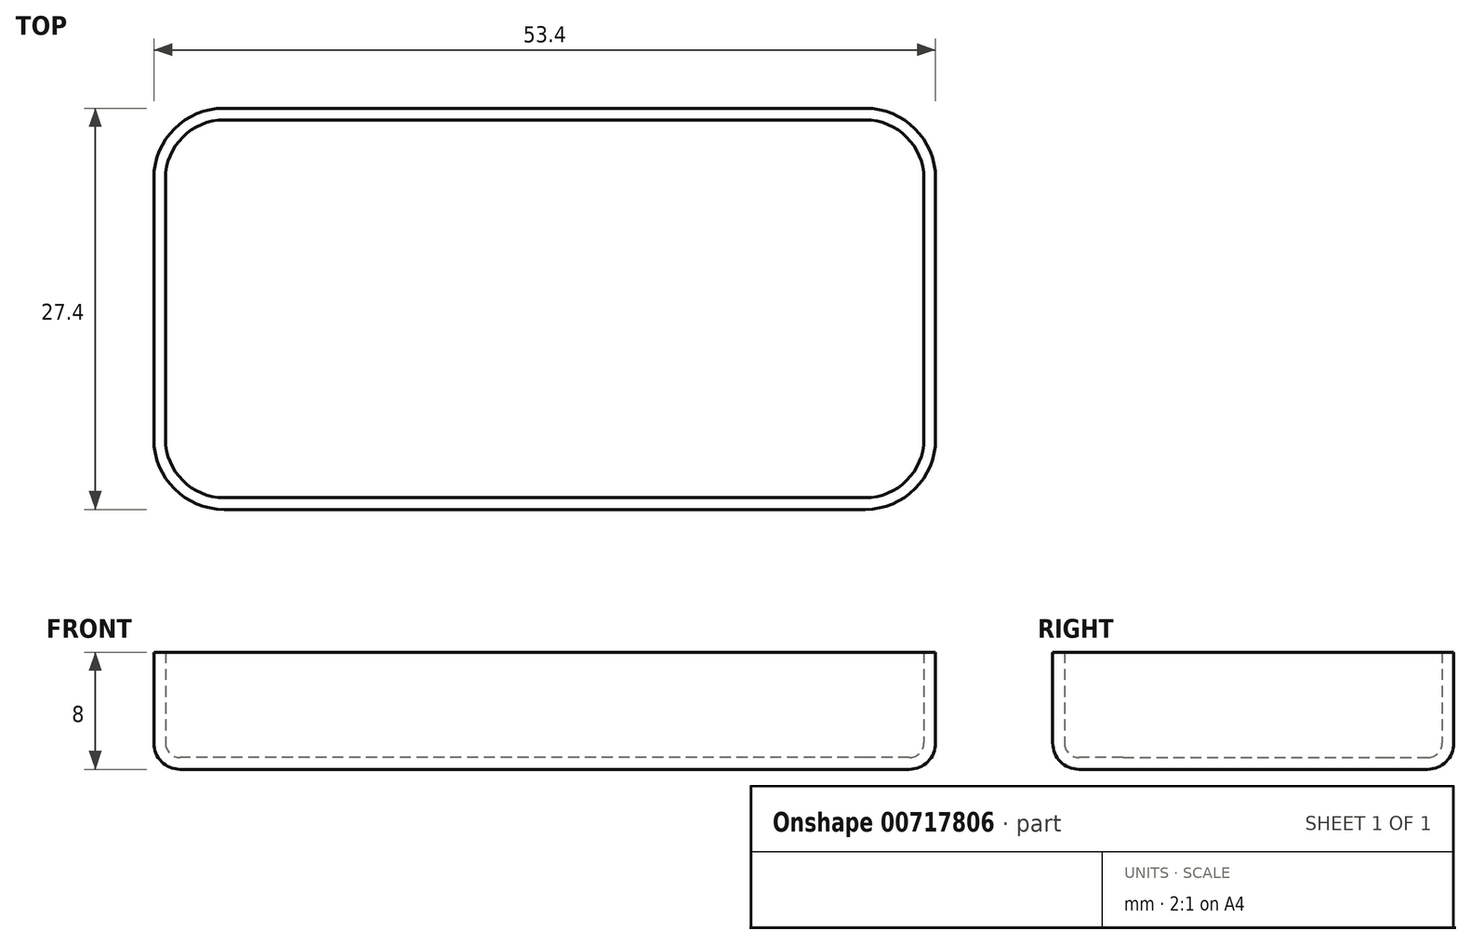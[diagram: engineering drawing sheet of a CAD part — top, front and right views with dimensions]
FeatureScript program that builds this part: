
annotation { "Feature Type Name" : "Feature", "Feature Type Description" : "" }
export const myFeature = defineFeature(function(context is Context, id is Id, definition is map)
    precondition{}
    {
        {
            var Q0;
            Q0=qCreatedBy(makeId("Top.planeOp"),FACE);
            var sketch = newSketch(context, id + "F0", { "sketchPlane" : qUnion([Q0])});
            skLineSegment(sketch, "E0.bottom", {"start": v(26.7, -13.7) * mm, "end": v(-26.7, -13.7) * mm});
            skLineSegment(sketch, "E0.top", {"start": v(26.7, 13.7) * mm, "end": v(-26.7, 13.7) * mm});
            skLineSegment(sketch, "E0.left", {"start": v(26.7, -13.7) * mm, "end": v(26.7, 13.7) * mm});
            skLineSegment(sketch, "E0.right", {"start": v(-26.7, -13.7) * mm, "end": v(-26.7, 13.7) * mm});
            skPoint(sketch, "E0.middle", {"position": v(0, 0) * mm});
            skLineSegment(sketch, "E1.bottom", {"start": v(-25.9, 12.9) * mm, "end": v(25.9, 12.9) * mm});
            skLineSegment(sketch, "E1.top", {"start": v(-25.9, -12.9) * mm, "end": v(25.9, -12.9) * mm});
            skLineSegment(sketch, "E1.left", {"start": v(-25.9, 12.9) * mm, "end": v(-25.9, -12.9) * mm});
            skLineSegment(sketch, "E1.right", {"start": v(25.9, 12.9) * mm, "end": v(25.9, -12.9) * mm});
            skSolve(sketch);
        }
        {
            var Q0;
            Q0=qSketchRegion(id+"F0",true);
            var Q1;
            Q1=makeQuery(id+"F0.imprint","IMPRINT",FACE,{"disambiguationData":[TD([[makeQuery(id+"F0.imprint","IMPRINT",EDGE,{"derivedFrom":sQuery(id+"F0.wireOp",EDGE,"E1.bottom")}),-1.0]])]});
            extrude(context, id + "F1", {"entities" : qUnion([Q0, Q1]), "depth" : .8 * mm, "offsetDistance" : 25 * mm});
        }
        {
            var Q0;
            Q0=makeQuery(id+"F0.imprint","IMPRINT",FACE,{"disambiguationData":[TD([[makeQuery(id+"F0.imprint","IMPRINT",EDGE,{"derivedFrom":sQuery(id+"F0.wireOp",EDGE,"E0.bottom")}),-1.0]])]});
            extrude(context, id + "F2", {"entities" : qUnion([Q0]), "operationType" : NewBodyOperationType.ADD, "depth" : 8 * mm, "offsetDistance" : 25 * mm});
        }
        {
            var Q0;
            Q0=makeQuery(id+"F2.opExtrude","SWEPT_EDGE",EDGE,{"disambiguationData":[OSD([sQuery(id+"F0.wireOp",EDGE,"E1.bottom"),sQuery(id+"F0.wireOp",EDGE,"E1.left")])]});
            var Q1;
            Q1=makeQuery(id+"F2.opExtrude","SWEPT_EDGE",EDGE,{"disambiguationData":[OSD([sQuery(id+"F0.wireOp",EDGE,"E1.bottom"),sQuery(id+"F0.wireOp",EDGE,"E1.right")])]});
            var Q2;
            Q2=makeQuery(id+"F2.opExtrude","SWEPT_EDGE",EDGE,{"disambiguationData":[OSD([sQuery(id+"F0.wireOp",EDGE,"E1.top"),sQuery(id+"F0.wireOp",EDGE,"E1.right")])]});
            var Q3;
            Q3=makeQuery(id+"F2.opExtrude","SWEPT_EDGE",EDGE,{"disambiguationData":[OSD([sQuery(id+"F0.wireOp",EDGE,"E1.top"),sQuery(id+"F0.wireOp",EDGE,"E1.left")])]});
            fillet(context, id + "F3", {"entities" : qUnion([Q0, Q1, Q2, Q3]), "radius" : 4 * mm, "tangentPropagation" : true, "allowEdgeOverflow" : false});
        }
        {
            var Q0;
            {var subQ0=sQuery(id+"F0.wireOp",EDGE,"E0.left");var subQ1=sQuery(id+"F0.wireOp",EDGE,"E0.top");Q0=makeQuery(id+"F2.boolean.opBoolean","MERGE",EDGE,{"derivedFrom":[makeQuery(id+"F1.opExtrude","SWEPT_EDGE",EDGE,{"disambiguationData":[OSD([subQ1,subQ0])]}),makeQuery(id+"F2.opExtrude","SWEPT_EDGE",EDGE,{"disambiguationData":[OSD([subQ1,subQ0])]})]});}
            var Q1;
            {var subQ0=sQuery(id+"F0.wireOp",EDGE,"E0.left");var subQ1=sQuery(id+"F0.wireOp",EDGE,"E0.bottom");Q1=makeQuery(id+"F2.boolean.opBoolean","MERGE",EDGE,{"derivedFrom":[makeQuery(id+"F1.opExtrude","SWEPT_EDGE",EDGE,{"disambiguationData":[OSD([subQ1,subQ0])]}),makeQuery(id+"F2.opExtrude","SWEPT_EDGE",EDGE,{"disambiguationData":[OSD([subQ1,subQ0])]})]});}
            var Q2;
            {var subQ0=sQuery(id+"F0.wireOp",EDGE,"E0.right");var subQ1=sQuery(id+"F0.wireOp",EDGE,"E0.top");Q2=makeQuery(id+"F2.boolean.opBoolean","MERGE",EDGE,{"derivedFrom":[makeQuery(id+"F1.opExtrude","SWEPT_EDGE",EDGE,{"disambiguationData":[OSD([subQ1,subQ0])]}),makeQuery(id+"F2.opExtrude","SWEPT_EDGE",EDGE,{"disambiguationData":[OSD([subQ1,subQ0])]})]});}
            var Q3;
            {var subQ0=sQuery(id+"F0.wireOp",EDGE,"E0.right");var subQ1=sQuery(id+"F0.wireOp",EDGE,"E0.bottom");Q3=makeQuery(id+"F2.boolean.opBoolean","MERGE",EDGE,{"derivedFrom":[makeQuery(id+"F1.opExtrude","SWEPT_EDGE",EDGE,{"disambiguationData":[OSD([subQ1,subQ0])]}),makeQuery(id+"F2.opExtrude","SWEPT_EDGE",EDGE,{"disambiguationData":[OSD([subQ1,subQ0])]})]});}
            fillet(context, id + "F4", {"entities" : qUnion([Q0, Q1, Q2, Q3]), "radius" : 4.8 * mm, "tangentPropagation" : true, "allowEdgeOverflow" : false});
        }
        {
            var Q0;
            Q0=makeQuery(id+"F2.boolean.opBoolean","INTERSECT",EDGE,{"derivedFrom":[makeQuery(id+"F1.opExtrude","CAP_FACE",FACE,{"disambiguationData":[OSD([sQuery(id+"F0.wireOp",EDGE,"E0.bottom"),sQuery(id+"F0.wireOp",EDGE,"E0.top"),sQuery(id+"F0.wireOp",EDGE,"E0.left"),sQuery(id+"F0.wireOp",EDGE,"E0.right")])],"isStart":false}),makeQuery(id+"F2.opExtrude","SWEPT_FACE",FACE,{"disambiguationData":[OSD([sQuery(id+"F0.wireOp",EDGE,"E1.bottom")])]})]});
            fillet(context, id + "F5", {"entities" : qUnion([Q0]), "radius" : 1 * mm, "tangentPropagation" : true, "allowEdgeOverflow" : false});
        }
        {
            var Q0;
            Q0=makeQuery(id+"F1.opExtrude","CAP_EDGE",EDGE,{"disambiguationData":[OSD([sQuery(id+"F0.wireOp",EDGE,"E0.top")])],"isStart":true});
            fillet(context, id + "F6", {"entities" : qUnion([Q0]), "radius" : 1.8 * mm, "tangentPropagation" : true, "allowEdgeOverflow" : false});
        }
    });
